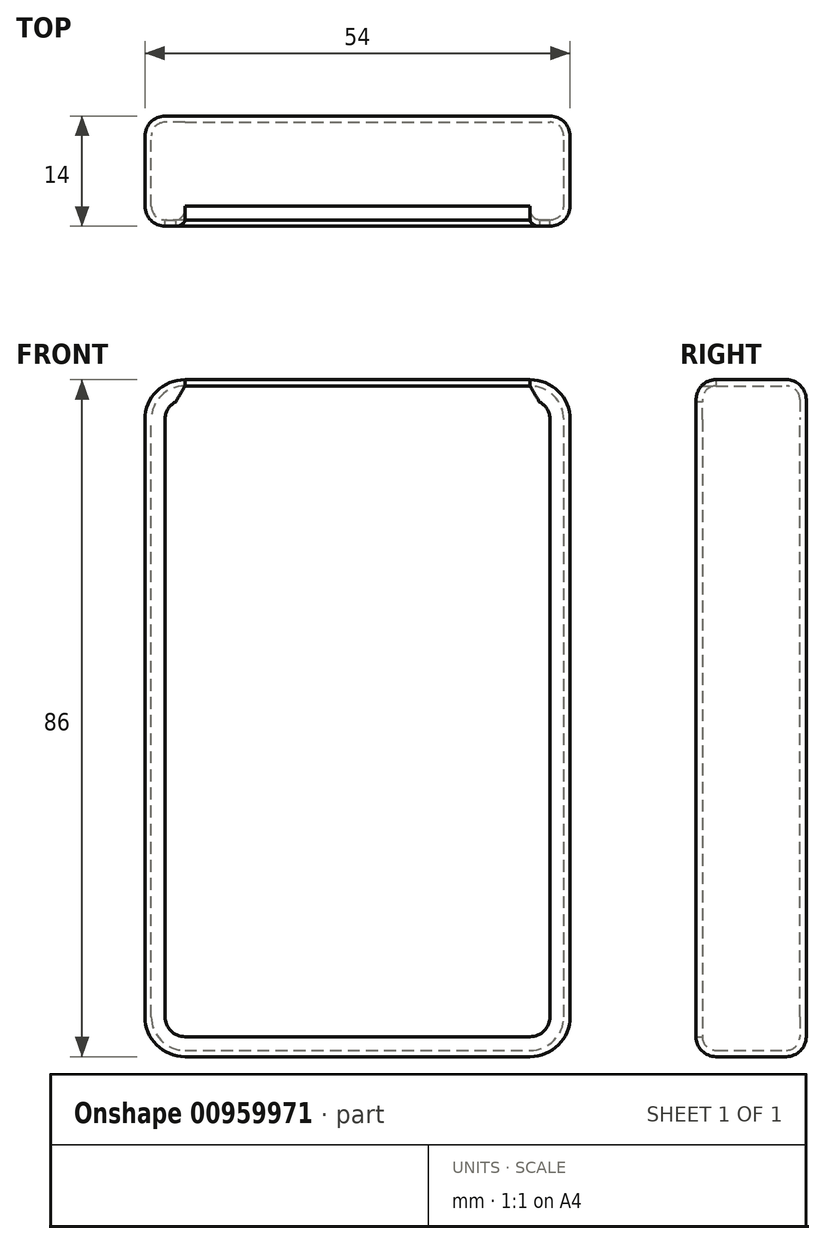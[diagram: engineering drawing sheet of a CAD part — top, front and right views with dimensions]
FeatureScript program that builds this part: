
annotation { "Feature Type Name" : "Feature", "Feature Type Description" : "" }
export const myFeature = defineFeature(function(context is Context, id is Id, definition is map)
    precondition{}
    {
        {
            var Q0;
            Q0=qCreatedBy(makeId("Front.planeOp"),FACE);
            var sketch = newSketch(context, id + "F0", { "sketchPlane" : qUnion([Q0])});
            skLineSegment(sketch, "E0.bottom", {"start": v(33.04, 48.44) * mm, "end": v(-20.96, 48.44) * mm});
            skLineSegment(sketch, "E0.top", {"start": v(33.04, -37.56) * mm, "end": v(-20.96, -37.56) * mm});
            skLineSegment(sketch, "E0.left", {"start": v(33.04, 48.44) * mm, "end": v(33.04, -37.56) * mm});
            skLineSegment(sketch, "E0.right", {"start": v(-20.96, 48.44) * mm, "end": v(-20.96, -37.56) * mm});
            skSolve(sketch);
        }
        {
            var Q0;
            Q0 = qSketchRegion(id + "F0", true);
            extrude(context, id + "F1", {"entities" : qUnion([Q0]), "oppositeDirection" : true, "depth" : 14 * mm, "offsetDistance" : 25.4 * mm});
        }
        {
            var Q0;
            Q0=makeQuery(id+"F1.opExtrude","SWEPT_EDGE",EDGE,{"disambiguationData":[OSD([sQuery(id+"F0.wireOp",EDGE,"E0.bottom"),sQuery(id+"F0.wireOp",EDGE,"E0.right")])]});
            fillet(context, id + "F2", {"entities" : qUnion([Q0]), "tangentPropagation" : true, "radius" : 5.08 * mm, "defaultsChanged" : false, "vertexSettings" : [], "allowEdgeOverflow" : false});
        }
        {
            var Q0;
            Q0=makeQuery(id+"F1.opExtrude","SWEPT_EDGE",EDGE,{"disambiguationData":[OSD([sQuery(id+"F0.wireOp",EDGE,"E0.bottom"),sQuery(id+"F0.wireOp",EDGE,"E0.left")])]});
            fillet(context, id + "F3", {"entities" : qUnion([Q0]), "tangentPropagation" : true, "radius" : 5.08 * mm, "defaultsChanged" : false, "vertexSettings" : [], "allowEdgeOverflow" : false});
        }
        {
            var Q0;
            Q0=makeQuery(id+"F1.opExtrude","SWEPT_EDGE",EDGE,{"disambiguationData":[OSD([sQuery(id+"F0.wireOp",EDGE,"E0.top"),sQuery(id+"F0.wireOp",EDGE,"E0.left")])]});
            fillet(context, id + "F4", {"entities" : qUnion([Q0]), "tangentPropagation" : true, "radius" : 5.08 * mm, "defaultsChanged" : false, "vertexSettings" : [], "allowEdgeOverflow" : false});
        }
        {
            var Q0;
            Q0=makeQuery(id+"F1.opExtrude","SWEPT_EDGE",EDGE,{"disambiguationData":[OSD([sQuery(id+"F0.wireOp",EDGE,"E0.top"),sQuery(id+"F0.wireOp",EDGE,"E0.right")])]});
            fillet(context, id + "F5", {"entities" : qUnion([Q0]), "tangentPropagation" : true, "radius" : 5.08 * mm, "defaultsChanged" : false, "vertexSettings" : [], "allowEdgeOverflow" : false});
        }
        {
            var Q0;
            Q0=makeQuery(id+"F1.opExtrude","CAP_EDGE",EDGE,{"disambiguationData":[OSD([sQuery(id+"F0.wireOp",EDGE,"E0.left")])],"isStart":true});
            fillet(context, id + "F6", {"entities" : qUnion([Q0]), "tangentPropagation" : true, "radius" : 2.54 * mm, "defaultsChanged" : true, "vertexSettings" : [], "allowEdgeOverflow" : false});
        }
        {
            var Q0;
            Q0=makeQuery(id+"F1.opExtrude","CAP_EDGE",EDGE,{"disambiguationData":[OSD([sQuery(id+"F0.wireOp",EDGE,"E0.left")])],"isStart":false});
            fillet(context, id + "F7", {"entities" : qUnion([Q0]), "tangentPropagation" : true, "radius" : 2.54 * mm, "defaultsChanged" : true, "vertexSettings" : [], "allowEdgeOverflow" : false});
        }
        {
            var Q0;
            Q0=makeQuery(id+"F1.opExtrude","CAP_FACE",FACE,{"disambiguationData":[OSD([sQuery(id+"F0.wireOp",EDGE,"E0.bottom"),sQuery(id+"F0.wireOp",EDGE,"E0.top"),sQuery(id+"F0.wireOp",EDGE,"E0.left"),sQuery(id+"F0.wireOp",EDGE,"E0.right")])],"isStart":true});
            var Q1;
            Q1=makeQuery(id+"F6.opFillet","BLEND_FACE",FACE,{"disambiguationData":[OSD([sQuery(id+"F0.wireOp",EDGE,"E0.bottom")])]});
            shell(context, id + "F8", {"entities" : qUnion([Q0, Q1]), "thickness" : .8 * mm});
        }
        {
            var Q0;
            {var subQ0=sQuery(id+"F0.wireOp",EDGE,"E0.right");var subQ1=sQuery(id+"F0.wireOp",EDGE,"E0.bottom");var subQ2=makeQuery(id+"F1.opExtrude","CAP_FACE",FACE,{"disambiguationData":[OSD([subQ1,sQuery(id+"F0.wireOp",EDGE,"E0.top"),sQuery(id+"F0.wireOp",EDGE,"E0.left"),subQ0])],"isStart":true});Q0=makeQuery(id+"F8.opShell","SHELL_CAP_EDGE",EDGE,{"derivedFrom":[makeQuery(id+"F6.opFillet","BLEND_VERTEX",VERTEX,{"blendedFrom":[makeQuery(id+"F2.opFillet","BLEND_EDGE",EDGE,{"blendedFrom":[makeQuery(id+"F1.opExtrude","SWEPT_EDGE",EDGE,{"disambiguationData":[OSD([subQ1,subQ0])]}),subQ2],"blendedInto":[subQ2]}),makeQuery(id+"F1.opExtrude","CAP_EDGE",EDGE,{"disambiguationData":[OSD([subQ1])],"isStart":true}),subQ2],"blendedInto":[subQ2]})]});}
            chamfer(context, id + "F9", {"entities" : qUnion([Q0]), "width" : 2.3 * mm, "tangentPropagation" : true});
        }
        {
            var Q0;
            {var subQ0=sQuery(id+"F0.wireOp",EDGE,"E0.left");var subQ1=sQuery(id+"F0.wireOp",EDGE,"E0.bottom");var subQ2=makeQuery(id+"F1.opExtrude","CAP_FACE",FACE,{"disambiguationData":[OSD([subQ1,sQuery(id+"F0.wireOp",EDGE,"E0.top"),subQ0,sQuery(id+"F0.wireOp",EDGE,"E0.right")])],"isStart":true});Q0=makeQuery(id+"F8.opShell","SHELL_CAP_EDGE",EDGE,{"derivedFrom":[makeQuery(id+"F6.opFillet","BLEND_VERTEX",VERTEX,{"blendedFrom":[makeQuery(id+"F3.opFillet","BLEND_EDGE",EDGE,{"blendedFrom":[makeQuery(id+"F1.opExtrude","SWEPT_EDGE",EDGE,{"disambiguationData":[OSD([subQ1,subQ0])]}),subQ2],"blendedInto":[subQ2]}),makeQuery(id+"F1.opExtrude","CAP_EDGE",EDGE,{"disambiguationData":[OSD([subQ1])],"isStart":true}),subQ2],"blendedInto":[subQ2]})]});}
            chamfer(context, id + "F10", {"entities" : qUnion([Q0]), "width" : 2.3 * mm, "tangentPropagation" : true});
        }
    });
